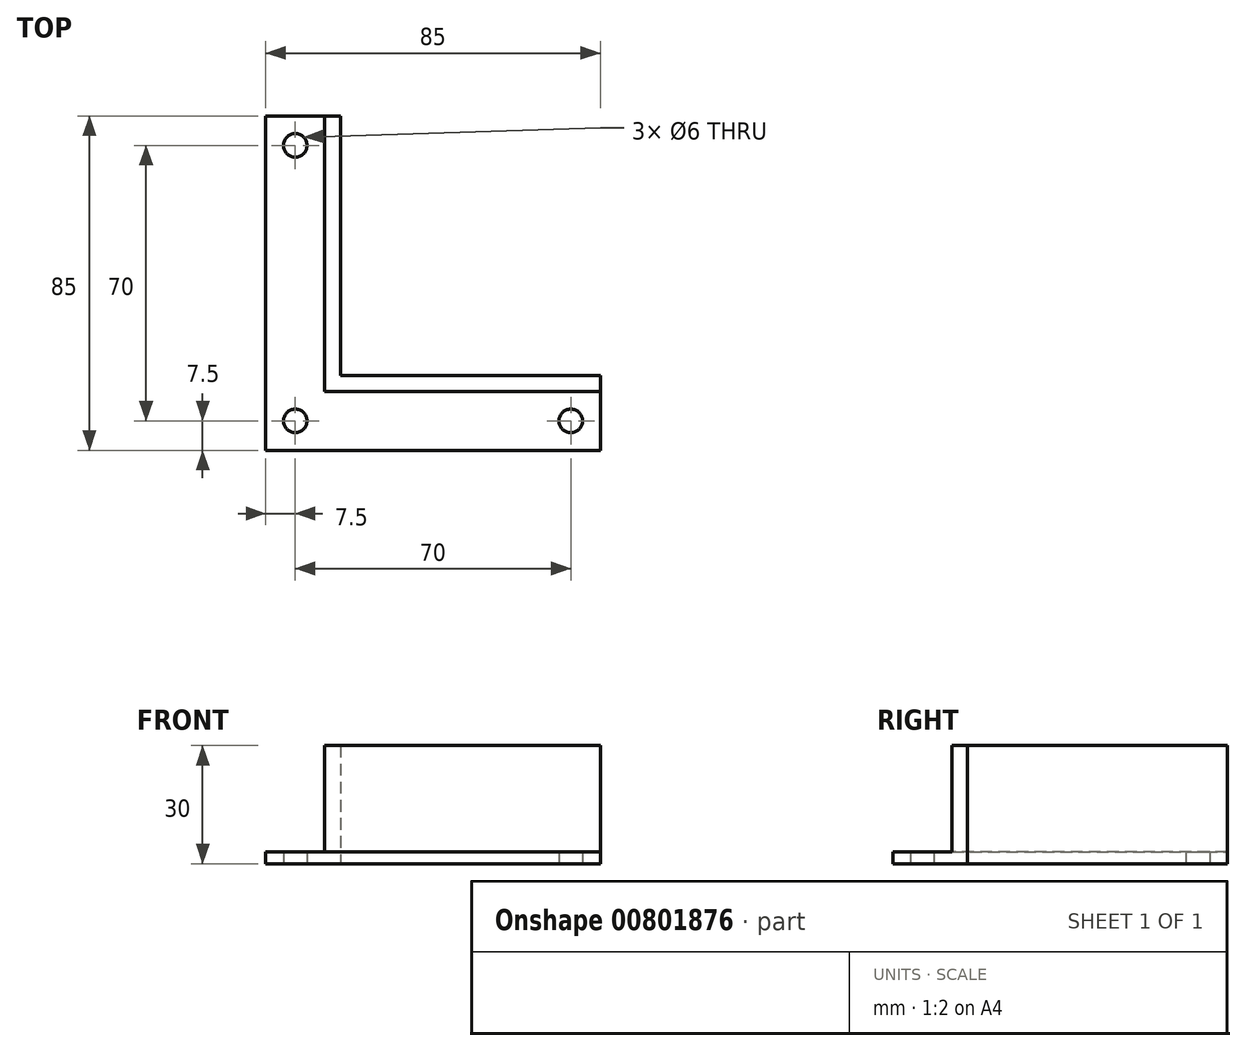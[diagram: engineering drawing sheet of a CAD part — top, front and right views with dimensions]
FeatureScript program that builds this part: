
annotation { "Feature Type Name" : "Feature", "Feature Type Description" : "" }
export const myFeature = defineFeature(function(context is Context, id is Id, definition is map)
    precondition{}
    {
        {
            var Q0;
            Q0=qCreatedBy(makeId("Top.planeOp"),FACE);
            var sketch = newSketch(context, id + "F0", { "sketchPlane" : qUnion([Q0])});
            skLineSegment(sketch, "E0.bottom", {"start": v(0, 0) * mm, "end": v(4, 0) * mm});
            skLineSegment(sketch, "E0.top", {"start": v(0, 70) * mm, "end": v(4, 70) * mm});
            skLineSegment(sketch, "E0.left", {"start": v(0, 0) * mm, "end": v(0, 70) * mm});
            skLineSegment(sketch, "E0.right", {"start": v(4, 0) * mm, "end": v(4, 70) * mm});
            skLineSegment(sketch, "E1.bottom", {"start": v(0, 0) * mm, "end": v(70, 0) * mm});
            skLineSegment(sketch, "E1.top", {"start": v(0, 4) * mm, "end": v(70, 4) * mm});
            skLineSegment(sketch, "E1.left", {"start": v(0, 0) * mm, "end": v(0, 4) * mm});
            skLineSegment(sketch, "E1.right", {"start": v(70, 0) * mm, "end": v(70, 4) * mm});
            skLineSegment(sketch, "E2.bottom", {"start": v(0, 70) * mm, "end": v(-15, 70) * mm});
            skLineSegment(sketch, "E2.top", {"start": v(0, -15) * mm, "end": v(-15, -15) * mm});
            skLineSegment(sketch, "E2.left", {"start": v(0, 70) * mm, "end": v(0, -15) * mm});
            skLineSegment(sketch, "E2.right", {"start": v(-15, 70) * mm, "end": v(-15, -15) * mm});
            skLineSegment(sketch, "E3.bottom", {"start": v(0, -15) * mm, "end": v(70, -15) * mm});
            skLineSegment(sketch, "E3.left", {"start": v(0, -15) * mm, "end": v(0, 0) * mm});
            skLineSegment(sketch, "E3.right", {"start": v(70, -15) * mm, "end": v(70, 0) * mm});
            skLineSegment(sketch, "E4", {"start": v(-7.5, -31.36) * mm, "end": v(-7.5, 97.5) * mm, "construction": true});
            skLineSegment(sketch, "E5", {"start": v(-37.43, -7.5) * mm, "end": v(100.16, -7.5) * mm, "construction": true});
            skCircle(sketch, "E6", {"center": v(-7.5, -7.5) * mm, "radius": 3 * mm});
            skCircle(sketch, "E7", {"center": v(-7.5, 62.5) * mm, "radius": 3 * mm});
            skCircle(sketch, "E8", {"center": v(62.5, -7.5) * mm, "radius": 3 * mm});
            skSolve(sketch);
        }
        {
            var Q0;
            {var subQ0=sQuery(id+"F0.wireOp",EDGE,"E0.top");Q0=makeQuery(id+"F0.imprint","IMPRINT",FACE,{"disambiguationData":[TD([[makeQuery(id+"F0.imprint","IMPRINT",EDGE,{"derivedFrom":subQ0}),-1.0]])]});}
            var Q1;
            {var subQ0=sQuery(id+"F0.wireOp",EDGE,"E1.bottom");Q1=makeQuery(id+"F0.imprint","IMPRINT",FACE,{"disambiguationData":[TD([[makeQuery(id+"F0.imprint","IMPRINT",EDGE,{"derivedFrom":subQ0}),1.0]])]});}
            var Q2;
            {var subQ0=sQuery(id+"F0.wireOp",EDGE,"E0.bottom");Q2=makeQuery(id+"F0.imprint","IMPRINT",FACE,{"disambiguationData":[TD([[makeQuery(id+"F0.imprint","IMPRINT",EDGE,{"derivedFrom":subQ0}),1.0]])]});}
            extrude(context, id + "F1", {"entities" : qUnion([Q0, Q1, Q2]), "depth" : 30 * mm, "offsetDistance" : 25 * mm});
        }
        {
            var Q0;
            {var subQ0=sQuery(id+"F0.wireOp",EDGE,"E2.bottom");Q0=makeQuery(id+"F0.imprint","IMPRINT",FACE,{"disambiguationData":[TD([[makeQuery(id+"F0.imprint","IMPRINT",EDGE,{"derivedFrom":subQ0}),1.0]])]});}
            var Q1;
            Q1=makeQuery(id+"F0.imprint","IMPRINT",FACE,{"disambiguationData":[TD([[makeQuery(id+"F0.imprint","IMPRINT",EDGE,{"derivedFrom":sQuery(id+"F0.wireOp",EDGE,"E0.bottom")}),-1.0]])]});
            extrude(context, id + "F2", {"entities" : qUnion([Q0, Q1]), "operationType" : NewBodyOperationType.ADD, "depth" : 3 * mm, "offsetDistance" : 25 * mm});
        }
    });
